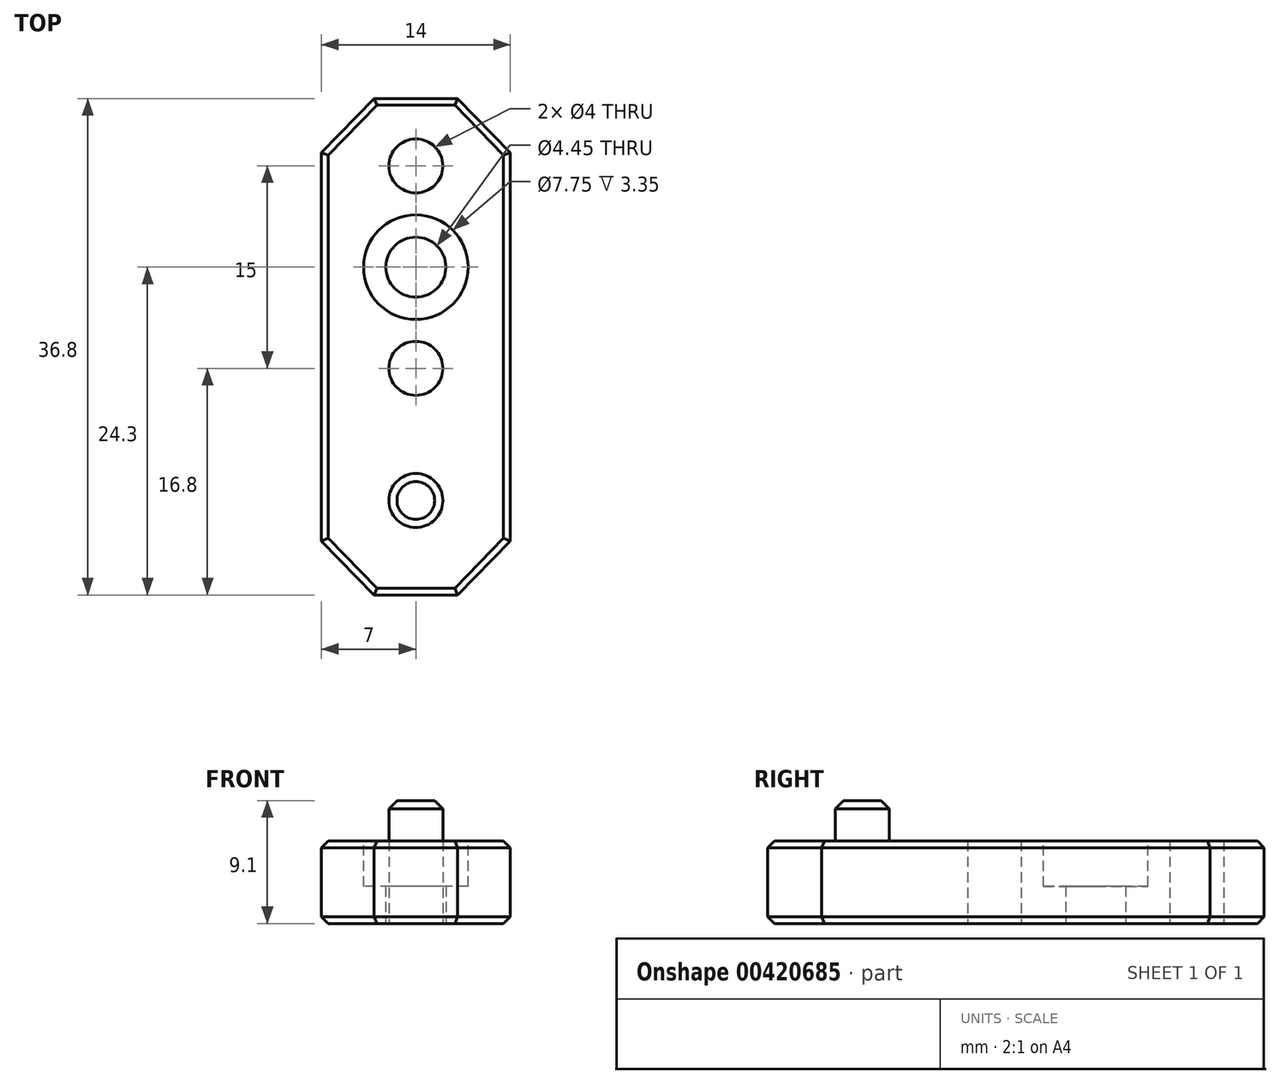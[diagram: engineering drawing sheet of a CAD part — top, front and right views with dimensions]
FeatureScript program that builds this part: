
annotation { "Feature Type Name" : "Feature", "Feature Type Description" : "" }
export const myFeature = defineFeature(function(context is Context, id is Id, definition is map)
    precondition{}
    {
        {
            var Q0;
            Q0=qCreatedBy(makeId("Top.planeOp"),FACE);
            var sketch = newSketch(context, id + "F0", { "sketchPlane" : qUnion([Q0])});
            skLineSegment(sketch, "E0", {"start": v(-7, 0) * mm, "end": v(-7, 14.4) * mm});
            skLineSegment(sketch, "E1", {"start": v(-7, 14.4) * mm, "end": v(-3.1, 18.4) * mm});
            skLineSegment(sketch, "E2", {"start": v(-3.1, 18.4) * mm, "end": v(0, 18.4) * mm});
            skLineSegment(sketch, "E3.MirrorCS", {"start": v(7, 0) * mm, "end": v(7, 14.4) * mm});
            skLineSegment(sketch, "E4.MirrorCS", {"start": v(7, 14.4) * mm, "end": v(3.1, 18.4) * mm});
            skLineSegment(sketch, "E5.MirrorCS", {"start": v(3.1, 18.4) * mm, "end": v(0, 18.4) * mm});
            skLineSegment(sketch, "E6.MirrorCS", {"start": v(-7, 0) * mm, "end": v(-7, -14.4) * mm});
            skLineSegment(sketch, "E7.MirrorCS", {"start": v(7, 0) * mm, "end": v(7, -14.4) * mm});
            skLineSegment(sketch, "E8.MirrorCS", {"start": v(7, -14.4) * mm, "end": v(3.1, -18.4) * mm});
            skLineSegment(sketch, "E9.MirrorCS", {"start": v(3.1, -18.4) * mm, "end": v(0, -18.4) * mm});
            skLineSegment(sketch, "E10.MirrorCS", {"start": v(-7, -14.4) * mm, "end": v(-3.1, -18.4) * mm});
            skLineSegment(sketch, "E11.MirrorCS", {"start": v(-3.1, -18.4) * mm, "end": v(0, -18.4) * mm});
            skCircle(sketch, "E12", {"center": v(0, 13.4) * mm, "radius": 2 * mm});
            skCircle(sketch, "E13", {"center": v(0, 5.9) * mm, "radius": 2.23 * mm});
            skCircle(sketch, "E14", {"center": v(0, -1.6) * mm, "radius": 2 * mm});
            skSolve(sketch);
        }
        {
            var Q0;
            Q0=makeQuery(id+"F0.imprint","IMPRINT",FACE,{"disambiguationData":[TD([[makeQuery(id+"F0.imprint","IMPRINT",EDGE,{"derivedFrom":sQuery(id+"F0.wireOp",EDGE,"E0")}),-1.0]])]});
            extrude(context, id + "F1", {"entities" : qUnion([Q0]), "depth" : 6.1 * mm});
        }
        {
            var Q0;
            Q0=makeQuery(id+"F1.opExtrude","CAP_FACE",FACE,{"disambiguationData":[OSD([sQuery(id+"F0.wireOp",EDGE,"E0"),sQuery(id+"F0.wireOp",EDGE,"E2"),sQuery(id+"F0.wireOp",EDGE,"E1"),sQuery(id+"F0.wireOp",EDGE,"E5.MirrorCS"),sQuery(id+"F0.wireOp",EDGE,"E3.MirrorCS"),sQuery(id+"F0.wireOp",EDGE,"E4.MirrorCS"),sQuery(id+"F0.wireOp",EDGE,"E6.MirrorCS"),sQuery(id+"F0.wireOp",EDGE,"E11.MirrorCS"),sQuery(id+"F0.wireOp",EDGE,"E10.MirrorCS"),sQuery(id+"F0.wireOp",EDGE,"E9.MirrorCS"),sQuery(id+"F0.wireOp",EDGE,"E7.MirrorCS"),sQuery(id+"F0.wireOp",EDGE,"E8.MirrorCS"),sQuery(id+"F0.wireOp",EDGE,"E12"),sQuery(id+"F0.wireOp",EDGE,"E13"),sQuery(id+"F0.wireOp",EDGE,"E14")])],"isStart":false});
            var sketch = newSketch(context, id + "F2", { "sketchPlane" : qUnion([Q0])});
            skCircle(sketch, "E15", {"center": v(0, 5.9) * mm, "radius": 3.87 * mm});
            skSolve(sketch);
        }
        {
            var Q0;
            Q0=makeQuery(id+"F2.imprint","IMPRINT",FACE,{"disambiguationData":[TD([[makeQuery(id+"F2.imprint","IMPRINT",EDGE,{"derivedFrom":sQuery(id+"F2.wireOp",EDGE,"E15")}),1.0]])]});
            extrude(context, id + "F3", {"entities" : qUnion([Q0]), "operationType" : NewBodyOperationType.REMOVE, "oppositeDirection" : true, "depth" : 3.35 * mm});
        }
        {
            var Q0;
            Q0=makeQuery(id+"F1.opExtrude","CAP_FACE",FACE,{"disambiguationData":[OSD([sQuery(id+"F0.wireOp",EDGE,"E0"),sQuery(id+"F0.wireOp",EDGE,"E2"),sQuery(id+"F0.wireOp",EDGE,"E1"),sQuery(id+"F0.wireOp",EDGE,"E5.MirrorCS"),sQuery(id+"F0.wireOp",EDGE,"E3.MirrorCS"),sQuery(id+"F0.wireOp",EDGE,"E4.MirrorCS"),sQuery(id+"F0.wireOp",EDGE,"E6.MirrorCS"),sQuery(id+"F0.wireOp",EDGE,"E11.MirrorCS"),sQuery(id+"F0.wireOp",EDGE,"E10.MirrorCS"),sQuery(id+"F0.wireOp",EDGE,"E9.MirrorCS"),sQuery(id+"F0.wireOp",EDGE,"E7.MirrorCS"),sQuery(id+"F0.wireOp",EDGE,"E8.MirrorCS"),sQuery(id+"F0.wireOp",EDGE,"E12"),sQuery(id+"F0.wireOp",EDGE,"E13"),sQuery(id+"F0.wireOp",EDGE,"E14")])],"isStart":false});
            var sketch = newSketch(context, id + "F4", { "sketchPlane" : qUnion([Q0])});
            skCircle(sketch, "E16", {"center": v(0, -11.4) * mm, "radius": 2 * mm});
            skSolve(sketch);
        }
        {
            var Q0;
            Q0=makeQuery(id+"F4.imprint","IMPRINT",FACE,{"disambiguationData":[TD([[makeQuery(id+"F4.imprint","IMPRINT",EDGE,{"derivedFrom":sQuery(id+"F4.wireOp",EDGE,"E16")}),1.0]])]});
            extrude(context, id + "F5", {"entities" : qUnion([Q0]), "operationType" : NewBodyOperationType.ADD, "depth" : 3 * mm});
        }
        {
            var Q0;
            Q0=makeQuery(id+"F5.opExtrude","CAP_EDGE",EDGE,{"disambiguationData":[OSD([sQuery(id+"F4.wireOp",EDGE,"E16")])],"isStart":false});
            chamfer(context, id + "F6", {"entities" : qUnion([Q0]), "width" : 0.6 * mm, "tangentPropagation" : true});
        }
        {
            var Q0;
            Q0=makeQuery(id+"F1.opExtrude","CAP_EDGE",EDGE,{"disambiguationData":[OSD([sQuery(id+"F0.wireOp",EDGE,"E0"),sQuery(id+"F0.wireOp",EDGE,"E6.MirrorCS")])],"isStart":true});
            var Q1;
            Q1=makeQuery(id+"F1.opExtrude","CAP_EDGE",EDGE,{"disambiguationData":[OSD([sQuery(id+"F0.wireOp",EDGE,"E10.MirrorCS")])],"isStart":true});
            var Q2;
            Q2=makeQuery(id+"F1.opExtrude","CAP_EDGE",EDGE,{"disambiguationData":[OSD([sQuery(id+"F0.wireOp",EDGE,"E11.MirrorCS"),sQuery(id+"F0.wireOp",EDGE,"E9.MirrorCS")])],"isStart":true});
            var Q3;
            Q3=makeQuery(id+"F1.opExtrude","CAP_EDGE",EDGE,{"disambiguationData":[OSD([sQuery(id+"F0.wireOp",EDGE,"E8.MirrorCS")])],"isStart":true});
            var Q4;
            Q4=makeQuery(id+"F1.opExtrude","CAP_EDGE",EDGE,{"disambiguationData":[OSD([sQuery(id+"F0.wireOp",EDGE,"E3.MirrorCS"),sQuery(id+"F0.wireOp",EDGE,"E7.MirrorCS")])],"isStart":true});
            var Q5;
            Q5=makeQuery(id+"F1.opExtrude","CAP_EDGE",EDGE,{"disambiguationData":[OSD([sQuery(id+"F0.wireOp",EDGE,"E4.MirrorCS")])],"isStart":true});
            var Q6;
            Q6=makeQuery(id+"F1.opExtrude","CAP_EDGE",EDGE,{"disambiguationData":[OSD([sQuery(id+"F0.wireOp",EDGE,"E2"),sQuery(id+"F0.wireOp",EDGE,"E5.MirrorCS")])],"isStart":true});
            var Q7;
            Q7=makeQuery(id+"F1.opExtrude","CAP_EDGE",EDGE,{"disambiguationData":[OSD([sQuery(id+"F0.wireOp",EDGE,"E1")])],"isStart":true});
            var Q8;
            Q8=makeQuery(id+"F1.opExtrude","CAP_EDGE",EDGE,{"disambiguationData":[OSD([sQuery(id+"F0.wireOp",EDGE,"E8.MirrorCS")])],"isStart":false});
            var Q9;
            Q9=makeQuery(id+"F1.opExtrude","CAP_EDGE",EDGE,{"disambiguationData":[OSD([sQuery(id+"F0.wireOp",EDGE,"E11.MirrorCS"),sQuery(id+"F0.wireOp",EDGE,"E9.MirrorCS")])],"isStart":false});
            var Q10;
            Q10=makeQuery(id+"F1.opExtrude","CAP_EDGE",EDGE,{"disambiguationData":[OSD([sQuery(id+"F0.wireOp",EDGE,"E10.MirrorCS")])],"isStart":false});
            var Q11;
            Q11=makeQuery(id+"F1.opExtrude","CAP_EDGE",EDGE,{"disambiguationData":[OSD([sQuery(id+"F0.wireOp",EDGE,"E0"),sQuery(id+"F0.wireOp",EDGE,"E6.MirrorCS")])],"isStart":false});
            var Q12;
            Q12=makeQuery(id+"F1.opExtrude","CAP_EDGE",EDGE,{"disambiguationData":[OSD([sQuery(id+"F0.wireOp",EDGE,"E1")])],"isStart":false});
            var Q13;
            Q13=makeQuery(id+"F1.opExtrude","CAP_EDGE",EDGE,{"disambiguationData":[OSD([sQuery(id+"F0.wireOp",EDGE,"E2"),sQuery(id+"F0.wireOp",EDGE,"E5.MirrorCS")])],"isStart":false});
            var Q14;
            Q14=makeQuery(id+"F1.opExtrude","CAP_EDGE",EDGE,{"disambiguationData":[OSD([sQuery(id+"F0.wireOp",EDGE,"E4.MirrorCS")])],"isStart":false});
            var Q15;
            Q15=makeQuery(id+"F1.opExtrude","CAP_EDGE",EDGE,{"disambiguationData":[OSD([sQuery(id+"F0.wireOp",EDGE,"E3.MirrorCS"),sQuery(id+"F0.wireOp",EDGE,"E7.MirrorCS")])],"isStart":false});
            chamfer(context, id + "F7", {"entities" : qUnion([Q0, Q1, Q2, Q3, Q4, Q5, Q6, Q7, Q8, Q9, Q10, Q11, Q12, Q13, Q14, Q15]), "width" : 0.5 * mm, "tangentPropagation" : true});
        }
    });
